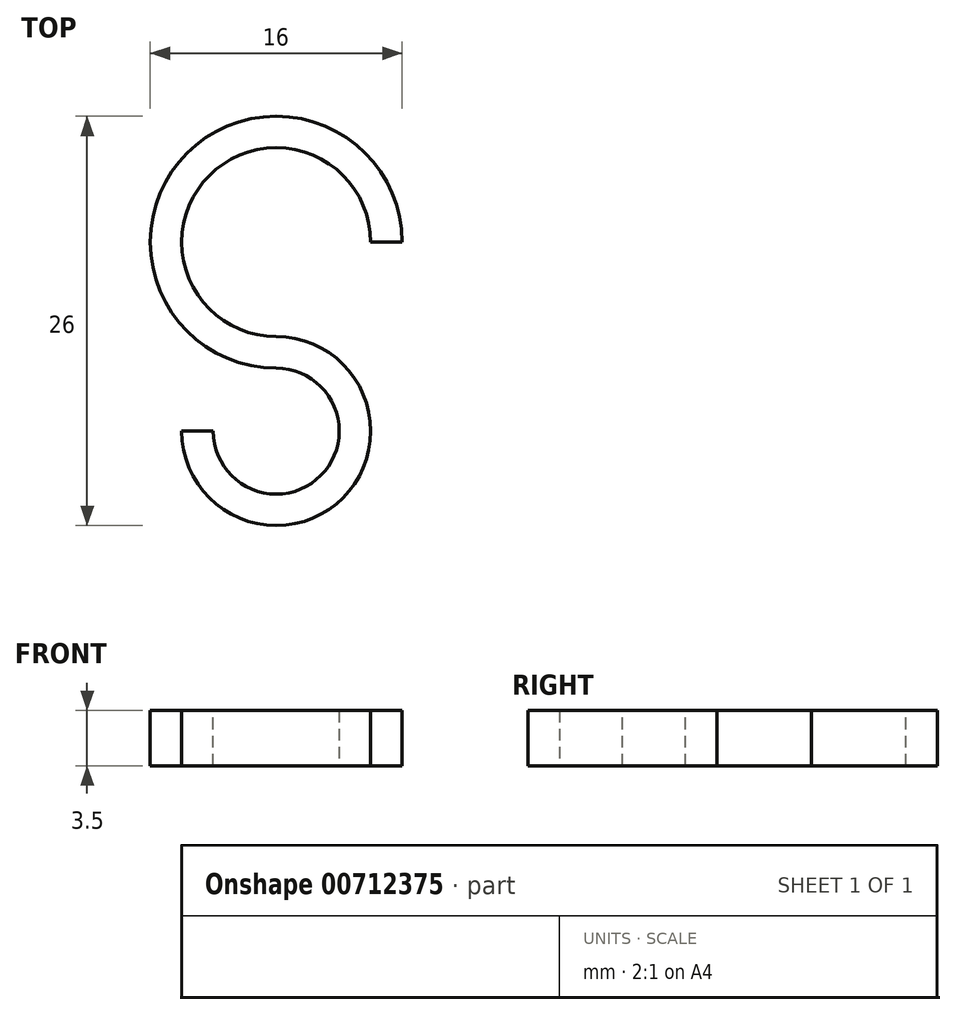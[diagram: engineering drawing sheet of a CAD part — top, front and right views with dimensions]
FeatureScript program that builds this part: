
annotation { "Feature Type Name" : "Feature", "Feature Type Description" : "" }
export const myFeature = defineFeature(function(context is Context, id is Id, definition is map)
    precondition{}
    {
        {
            var Q0;
            Q0=qCreatedBy(makeId("Top.planeOp"),FACE);
            var sketch = newSketch(context, id + "F0", { "sketchPlane" : qUnion([Q0])});
            skArc(sketch, "E0", {"start": v(-5, -12) * mm, "mid": v(3.54, -15.54) * mm, "end": v(0, -7) * mm});
            skArc(sketch, "E1", {"start": v(0, -7) * mm, "mid": v(-4.95, 4.95) * mm, "end": v(7, 0) * mm});
            skLineSegment(sketch, "E2", {"start": v(0, 0) * mm, "end": v(0, -12) * mm, "construction": true});
            skLineSegment(sketch, "E3", {"start": v(0, 0) * mm, "end": v(7, 0) * mm, "construction": true});
            skLineSegment(sketch, "E4", {"start": v(0, -12) * mm, "end": v(-5, -12) * mm, "construction": true});
            skSolve(sketch);
        }
        {
            var Q0;
            Q0=qCreatedBy(makeId("Front.planeOp"),FACE);
            var sketch = newSketch(context, id + "F1", { "sketchPlane" : qUnion([Q0])});
            skLineSegment(sketch, "E5.bottom", {"start": v(8, -1.75) * mm, "end": v(6, -1.75) * mm});
            skLineSegment(sketch, "E5.top", {"start": v(8, 1.75) * mm, "end": v(6, 1.75) * mm});
            skLineSegment(sketch, "E5.left", {"start": v(8, -1.75) * mm, "end": v(8, 1.75) * mm});
            skLineSegment(sketch, "E5.right", {"start": v(6, -1.75) * mm, "end": v(6, 1.75) * mm});
            skPoint(sketch, "E5.middle", {"position": v(7, 0) * mm});
            skSolve(sketch);
        }
        {
            var Q0;
            Q0=makeQuery(id+"F1.imprint","IMPRINT",FACE,{"disambiguationData":[TD([[makeQuery(id+"F1.imprint","IMPRINT",EDGE,{"derivedFrom":sQuery(id+"F1.wireOp",EDGE,"E5.bottom")}),-1.0]])]});
            var Q1;
            Q1 = qConstructionFilter(qBodyType(qCreatedBy(id + "F0" ,EDGE), BodyType.WIRE), ConstructionObject.NO);
            sweep(context, id + "F2", {"profiles" : qUnion([Q0]), "path" : qUnion([Q1])});
        }
    });
